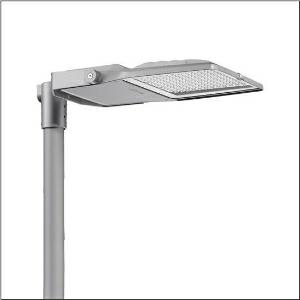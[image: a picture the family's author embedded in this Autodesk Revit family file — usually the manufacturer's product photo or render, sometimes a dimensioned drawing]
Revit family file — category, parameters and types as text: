
# Revit family: floodlight_fl_21_iq_midi___pl52_5xa7781e2d3a_77a1
name_source: partatom
category: Lighting Fixtures
units: mm (PartAtom-declared; Revit-internal decimal feet)

## family parameters
Cut with Voids When Loaded = No
Host = Face
Light Source = No
Part Type = Normal
Room Calculation Point = No
Round Connector Dimension = Use Diameter
Shared = No

## types (1)
- --- (1 x LED, 26850 lm, 208.1 W, 3000K)
    Apparent Load = 208 VA
    CIE Flux Codes = 26 60 98 100 100
    Color Rendering = 70
    Color Temperature = 3000K
    Default Elevation = 1800 mm
    Description = Floodlight FL 21 iQ midi, floodlight, primary light control with lens, of PMMA, primary optical cover: protective disc, of toughened safety glass, transparent, light distribution: PL52, light emission: direct distribution, installation type: surface-mounted, LED, High Power LED, rated luminous flux: 26.850lm, luminous efficacy: 129lm/W, light colour: 730, colour temperature: 3000K, control gear: iQ Comfort/DALI, control: optimised constant luminous flux control (CLO 2.0), Desk-Remote (wireless, voltage-free reading and setting of iQ features in the workshop via application-optimized NFC function/RFID function), Light-Fading, Smart-Wire, Night-Set, Lumen-Switch, Temp-Guard, Auto-Match, with terminal, 6-pole, mains connection: 220..240V, AC, 50/60Hz, start of lifetime: 208W, end of service life: 227W, reduction: 90W, luminaire housing, of diecast aluminium, powder-coated, Siteco® metallic grey (DB 702S), corrosivity category C5 mid according to DIN EN ISO 12944, suitable for swimming pools, chlorine-resistant, sealing non-destructively replaceable, please order mast flange separately, mast bracket, of steel, galvanised, powder-coated, Siteco® metallic grey (DB 702S), protection rating (complete): IP66, insulation class (complete): insulation class II (safety insulation), certification: CE, ENEC, VDE, protection symbol: D, impact resistance: IK08, permissible operating ambient temperature: -40..+40°C, permissible operating ambient temperature for outdoor applications: -40..+50°C, standard: DIN EN 12944, LABS conformity tested according to VDMA 24364:2018-05, packaging unit: 1 piece

Light Distribution: PL52
    Height = 76 mm
    Lamp = 1 x LED
    Lamp Light Flux = 26850 lm
    Lamp Power = 208.1 W
    Lamp count = 1
    Length = 657 mm
    Luminous efficacy = 129 lm/W
    Manufacturer = Siteco
    ModVariant = No
    Model = 5XA7781E2D3A
    Number of Poles = 1
    OnlyDefault = Yes
    Power Factor = 1
    Product Name = Floodlight FL 21 iQ midi | PL52
    Product group = floodlight | pylon annexe
    ProductGroupID = 6200
    Protection Class = Protection class II
    Protection Degree = IP 66
    RLX_Detail_Level = 1
    RLX_Emergency_Light_Flux = 0 lm
    RLX_Emergency_Type = 0
    RLX_Emergency_Type_DB = No
    RlxData = <blob elided: 154341 chars, md5=01d2530e>
    Socket = socket
    Standby Power = 0 W
    System Light Flux = 26850 lm
    System Power = 208 W
    Type Comments = factory setting: luminous flux: 100 % | dim-lin: 254 | 710 mA
    Type Image = l_1007123.jpg
    URL = http://relux.com
    VarID = @adj_106276
    Voltage = 0 V
    Weight = 0.00 kg
    Width = 442 mm

## geometry (parser evidence)
native form markers: Blend x4, Sweep x15
no freeform markers — native parametric forms only
